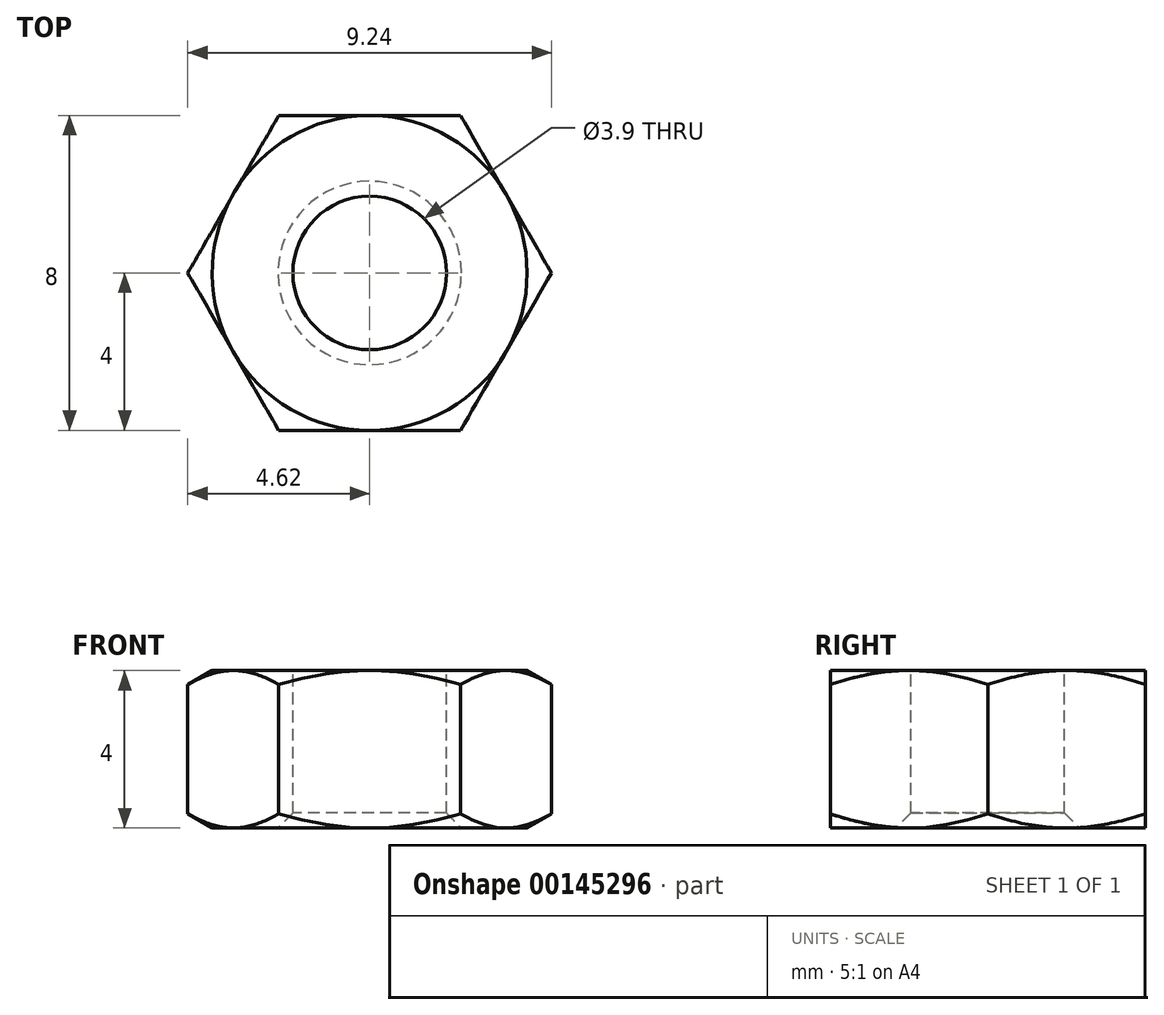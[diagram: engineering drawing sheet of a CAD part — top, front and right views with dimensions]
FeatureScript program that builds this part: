
annotation { "Feature Type Name" : "Feature", "Feature Type Description" : "" }
export const myFeature = defineFeature(function(context is Context, id is Id, definition is map)
    precondition{}
    {
        {
            var Q0;
            Q0=qCreatedBy(makeId("Top.planeOp"),FACE);
            var sketch = newSketch(context, id + "F0", { "sketchPlane" : qUnion([Q0])});
            skCircle(sketch, "E0", {"center": v(0, 0) * mm, "radius": 4 * mm, "construction": true});
            skLineSegment(sketch, "E1.0", {"start": v(-2.3, 4) * mm, "end": v(2.3, 4) * mm});
            skLineSegment(sketch, "E1.1", {"start": v(2.3, 4) * mm, "end": v(4.62, 0) * mm});
            skLineSegment(sketch, "E1.2", {"start": v(4.62, 0) * mm, "end": v(2.3, -4) * mm});
            skLineSegment(sketch, "E1.3", {"start": v(2.3, -4) * mm, "end": v(-2.3, -4) * mm});
            skLineSegment(sketch, "E1.4", {"start": v(-2.3, -4) * mm, "end": v(-4.62, 0) * mm});
            skLineSegment(sketch, "E1.5", {"start": v(-4.62, 0) * mm, "end": v(-2.3, 4) * mm});
            skPoint(sketch, "E1.0.midPoint", {"position": v(0, 4) * mm});
            skSolve(sketch);
        }
        {
            var Q0;
            Q0 = qSketchRegion(id + "F0", true);
            extrude(context, id + "F1", {"entities" : qUnion([Q0]), "endBound" : BoundingType.SYMMETRIC, "depth" : 4 * mm});
        }
        {
            var Q0;
            Q0=makeQuery(id+"F1.opExtrude","CAP_FACE",FACE,{"disambiguationData":[OSD([sQuery(id+"F0.wireOp",EDGE,"E1.0"),sQuery(id+"F0.wireOp",EDGE,"E1.1"),sQuery(id+"F0.wireOp",EDGE,"E1.2"),sQuery(id+"F0.wireOp",EDGE,"E1.3"),sQuery(id+"F0.wireOp",EDGE,"E1.4"),sQuery(id+"F0.wireOp",EDGE,"E1.5")])],"isStart":false});
            var sketch = newSketch(context, id + "F2", { "sketchPlane" : qUnion([Q0])});
            skLineSegment(sketch, "E2.0", {"start": v(-2.3, -4) * mm, "end": v(-4.62, 0) * mm, "construction": true});
            skLineSegment(sketch, "E3.0", {"start": v(2.3, 4) * mm, "end": v(4.62, 0) * mm, "construction": true});
            skLineSegment(sketch, "E4", {"start": v(-3.46, -2) * mm, "end": v(3.46, 2) * mm, "construction": true});
            skCircle(sketch, "E5", {"center": v(0, 0) * mm, "radius": 1.95 * mm});
            skSolve(sketch);
        }
        {
            var Q0;
            Q0 = qSketchRegion(id + "F2", true);
            extrude(context, id + "F3", {"entities" : qUnion([Q0]), "operationType" : NewBodyOperationType.REMOVE, "endBound" : BoundingType.THROUGH_ALL, "oppositeDirection" : true, "depth" : 25.4 * mm});
        }
        {
            var Q0;
            Q0=makeQuery(id+"F1.opExtrude","CAP_VERTEX",VERTEX,{"disambiguationData":[OSD([sQuery(id+"F0.wireOp",EDGE,"E1.0"),sQuery(id+"F0.wireOp",EDGE,"E1.1")])],"isStart":true});
            var Q1;
            Q1=makeQuery(id+"F1.opExtrude","CAP_VERTEX",VERTEX,{"disambiguationData":[OSD([sQuery(id+"F0.wireOp",EDGE,"E1.0"),sQuery(id+"F0.wireOp",EDGE,"E1.1")])],"isStart":false});
            var Q2;
            Q2=makeQuery(id+"F1.opExtrude","CAP_VERTEX",VERTEX,{"disambiguationData":[OSD([sQuery(id+"F0.wireOp",EDGE,"E1.4"),sQuery(id+"F0.wireOp",EDGE,"E1.5")])],"isStart":false});
            cPlane(context, id + "F4", {"entities" : qUnion([Q0, Q1, Q2]), "cplaneType" : CPlaneType.THREE_POINT, "offset" : 25.4 * mm, "width" : 152.4 * mm, "height" : 152.4 * mm});
        }
        {
            var Q0;
            Q0=qCreatedBy(id+"F4.planeOp",FACE);
            cPlane(context, id + "F5", {"entities" : qUnion([Q0]), "cplaneType" : CPlaneType.OFFSET, "offset" : 2.3 * mm, "oppositeDirection" : true, "width" : 152.4 * mm, "height" : 152.4 * mm});
        }
        {
            var Q0;
            Q0=qCreatedBy(id+"F5.planeOp",FACE);
            var sketch = newSketch(context, id + "F6", { "sketchPlane" : qUnion([Q0])});
            skLineSegment(sketch, "E6.0", {"start": v(4, 2) * mm, "end": v(5.64, 2) * mm});
            skLineSegment(sketch, "E7", {"start": v(4, 2) * mm, "end": v(5.64, 1.05) * mm});
            skLineSegment(sketch, "E8", {"start": v(5.64, 1.05) * mm, "end": v(5.64, 2) * mm});
            skPoint(sketch, "E9.orphan", {"position": v(0, 2) * mm});
            skLineSegment(sketch, "E10", {"start": v(0, 2) * mm, "end": v(0, -2.6) * mm, "construction": true});
            skSolve(sketch);
        }
        {
            var Q0;
            Q0=makeQuery(id+"F6.imprint","IMPRINT",FACE,{"disambiguationData":[TD([[makeQuery(id+"F6.imprint","IMPRINT",EDGE,{"derivedFrom":sQuery(id+"F6.wireOp",EDGE,"E6.0")}),-1.0]])]});
            var Q1;
            Q1=sQuery(id+"F6.wireOp",EDGE,"E10");
            revolve(context, id + "F7", {"operationType" : NewBodyOperationType.REMOVE, "entities" : qUnion([Q0]), "axis" : qUnion([Q1]), "revolveType" : RevolveType.FULL, "oppositeDirection" : true});
        }
        {
            var Q0;
            Q0=qCreatedBy(id+"F5.planeOp",FACE);
            var sketch = newSketch(context, id + "F8", { "sketchPlane" : qUnion([Q0])});
            skLineSegment(sketch, "E11.0", {"start": v(4, -2) * mm, "end": v(5.1, -2) * mm});
            skLineSegment(sketch, "E12", {"start": v(4, -2) * mm, "end": v(5.1, -1.37) * mm});
            skLineSegment(sketch, "E13", {"start": v(5.1, -1.37) * mm, "end": v(5.1, -2) * mm});
            skLineSegment(sketch, "E14.0", {"start": v(0, 1.64) * mm, "end": v(0, -2) * mm, "construction": true});
            skSolve(sketch);
        }
        {
            var Q0;
            Q0=makeQuery(id+"F8.imprint","IMPRINT",FACE,{"disambiguationData":[TD([[makeQuery(id+"F8.imprint","IMPRINT",EDGE,{"derivedFrom":sQuery(id+"F8.wireOp",EDGE,"E11.0")}),1.0]])]});
            var Q1;
            Q1=sQuery(id+"F8.wireOp",EDGE,"E13");
            var Q2;
            Q2=sQuery(id+"F8.wireOp",EDGE,"E14.0");
            revolve(context, id + "F9", {"operationType" : NewBodyOperationType.REMOVE, "entities" : qUnion([Q0]), "surfaceEntities" : qUnion([Q1]), "axis" : qUnion([Q2]), "revolveType" : RevolveType.FULL, "oppositeDirection" : true});
        }
        {
            var Q0;
            Q0=makeQuery(id+"F3.boolean.opBoolean","COPY",EDGE,{"derivedFrom":makeQuery(id+"F3.opExtrude","CAP_EDGE",EDGE,{"disambiguationData":[OSD([sQuery(id+"F2.wireOp",EDGE,"E5")])],"isStart":true})});
            var Q1;
            Q1=makeQuery(id+"F3.boolean.opBoolean","INTERSECT",EDGE,{"derivedFrom":[makeQuery(id+"F1.opExtrude","CAP_FACE",FACE,{"disambiguationData":[OSD([sQuery(id+"F0.wireOp",EDGE,"E1.0"),sQuery(id+"F0.wireOp",EDGE,"E1.1"),sQuery(id+"F0.wireOp",EDGE,"E1.2"),sQuery(id+"F0.wireOp",EDGE,"E1.3"),sQuery(id+"F0.wireOp",EDGE,"E1.4"),sQuery(id+"F0.wireOp",EDGE,"E1.5")])],"isStart":true}),makeQuery(id+"F3.opExtrude","SWEPT_FACE",FACE,{"disambiguationData":[OSD([sQuery(id+"F2.wireOp",EDGE,"E5")])]})]});
            chamfer(context, id + "F10", {"entities" : qUnion([Q0, Q1]), "width" : 0.38 * mm, "tangentPropagation" : true});
        }
    });
